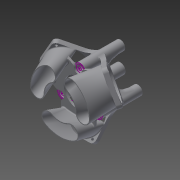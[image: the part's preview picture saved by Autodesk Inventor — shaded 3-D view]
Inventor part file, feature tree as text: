
AUTODESK INVENTOR PART (.ipt)
format: ipt  version: 2014 (Build 180170000, 170)  size: 2,420,736 bytes
history: native  units: mm
features: sketch x12, extrude x10, fillet x9, pattern_circular x4, projected_geometry x4, plane x3, loft x1, shell x1, boolean_combine x1, chamfer x1, other x1
ambient origin geometry x8: Origin, YZ Plane, XZ Plane, XY Plane, X Axis, Y Axis, Z Axis, Center Point
bodies: Solid1 (feature_tree), Solid2 (feature_tree), Solid5 (feature_tree), Solid7 (feature_tree)
feature tree (47):
  sketch  "Sketch1"  dims[d0=50.0mm d1=3.75mm]
  extrude  "Extrusion1"  Depth=3.75mm
  extrude  "Extrusion2"  Depth=12.0mm
  plane  "Work Plane1"
  extrude  "Extrusion3"  Depth=11.0mm
  extrude  "Extrusion4"  Depth=31.75mm TaperAngle=0.0deg
  fillet  "Fillet1"  Radius=9.0mm
  plane  "Work Plane2"
  extrude  "Extrusion5"  Depth=9.0mm
  sketch  "Sketch4"  dims[d12=20.0mm d13=31.75mm d14=0.0mm d15=9.0mm]
  extrude  "Extrusion6"  Depth=40.0mm
  plane  "Work Plane3"
  sketch  "Sketch6"  dims[d18=25.4mm d19=0.0mm d20=40.0mm]
  sketch  "Sketch7"  dims[d21=8.726646mm d22=5.0mm d23=5.0mm]
  loft  "Loft1"
  shell  "Shell1"  Thickness=5.0mm
  extrude  "Extrusion8"  Depth=10.0mm TaperAngle=0.0deg
  pattern_circular  "Circular Pattern1"  Count=4  [1 undecoded]
  pattern_circular  "Circular Pattern2"  Count=4  [1 undecoded]
  pattern_circular  "Circular Pattern3"  [2 undecoded]
  boolean_combine  "Combine1"
  fillet  "Fillet2"  Radius=3.0mm
  extrude  "Extrusion9"  Depth=5.0mm
  extrude  "Extrusion11"  Depth=5.0mm
  pattern_circular  "Circular Pattern4"  [2 undecoded]
  fillet  "Fillet7"  Radius=38.0mm
  fillet  "Fillet8"  Radius=40.0mm
  fillet  "Fillet3"  Radius=50.0mm
  fillet  "Fillet4"  Radius=42.5mm
  chamfer  "Chamfer2"  Distance=70.0mm
  fillet  "Fillet5"  [1 undecoded]
  extrude  "Extrusion12"  Depth=5.0mm
  fillet  "Fillet9"  Radius=2.0mm
  fillet  "Fillet10"  [1 undecoded]
  sketch  "Sketch2"  dims[d2=30.0mm d4=360.0deg d6=12.0mm]
  sketch  "Sketch3"  dims[d7=30.0mm d9=360.0deg d11=11.0mm]
  sketch  "Sketch5"  dims[d16=9.0mm d17=9.0mm]
  sketch  "3D Sketch1"
  other  "Work Point1"
  sketch  "Sketch9"  dims[d24=-25.0mm d25=10.0mm d26=0.0mm d27=40.0mm d28=0.0mm]
  projected_geometry  "Projected Loop2"
  sketch  "Sketch10"  dims[d29=5.0mm]
  sketch  "Sketch12"  dims[d30=5.0mm d31=40.0mm d32=0.0mm]
  projected_geometry  "Projected Loop6"
  projected_geometry  "Projected Loop7"
  sketch  "Sketch13"  dims[d33=32.0mm d34=32.0mm d35=3.0mm d36=3.0mm d37=3.0mm d38=3.0mm d39=38.0mm d40=40.0mm d41=0.0mm d42=50.0mm d43=42.5mm d44=70.0mm d45=60.0deg d46=2.0mm d47=2.0mm d48=0.0mm d49=90.0deg d50=0.0mm d51=90.0deg d54=1.0mm d55=2.5mm d56=0.0mm d57=30.0mm d58=360.0deg d60=30.0mm d61=360.0deg d63=30.0mm d64=360.0deg d66=10.0mm d67=35.0mm d68=2.0mm d69=0.0mm d75=3.0mm d76=1.0mm d77=2.0mm d78=2.0mm d79=13.962634mm d80=5.0mm d81=2.0mm d82=0.0mm d83=1.0mm d84=10.0mm d85=0.0mm d87=2.5mm d88=0.0mm d89=90.0deg d90=0.0mm d91=90.0deg d92=0.0mm d93=90.0deg d94=0.0mm d95=90.0deg d96=0.0mm d97=90.0deg d98=60.0mm d99=360.0deg d101=2.5mm d102=1.0mm d103=5.0mm d104=5.0mm]
  projected_geometry  "Project Cut Edges2"
note: 8 required parameter values undecoded (feature->parameter linkage not recoverable at this tier; creation-order binding heuristic only, values carry confidence <= 0.55)
